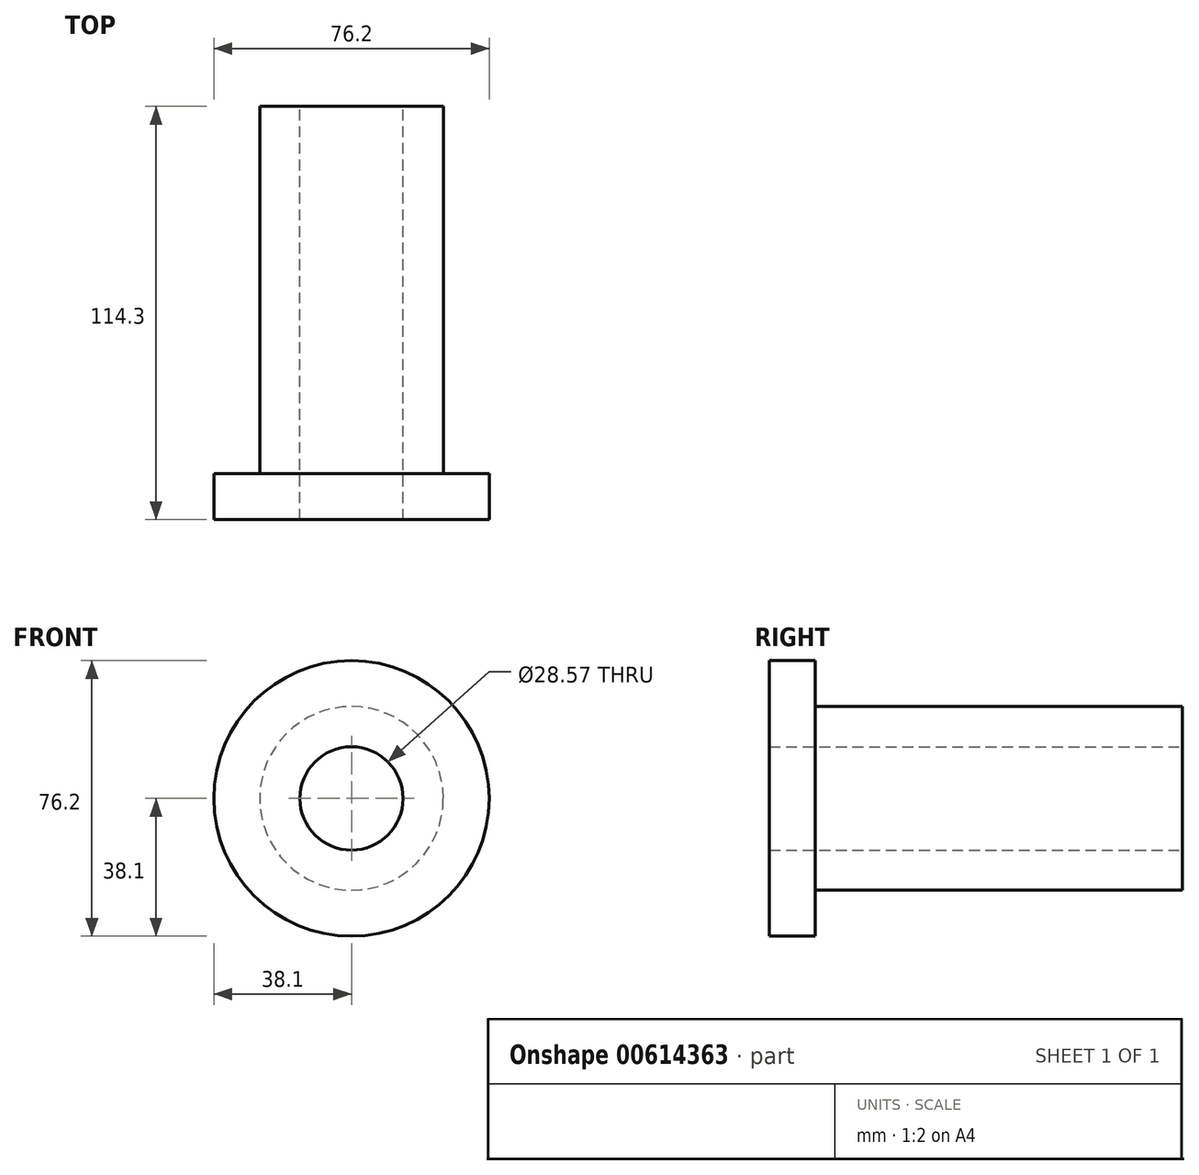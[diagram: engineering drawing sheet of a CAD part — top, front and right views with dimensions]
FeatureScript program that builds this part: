
annotation { "Feature Type Name" : "Feature", "Feature Type Description" : "" }
export const myFeature = defineFeature(function(context is Context, id is Id, definition is map)
    precondition{}
    {
        {
            var Q0;
            Q0=qCreatedBy(makeId("Front.planeOp"),FACE);
            var sketch = newSketch(context, id + "F0", { "sketchPlane" : qUnion([Q0])});
            skCircle(sketch, "E0", {"center": v(0, 0) * mm, "radius": 25.4 * mm});
            skCircle(sketch, "E1", {"center": v(0, 0) * mm, "radius": 14.29 * mm});
            skSolve(sketch);
        }
        {
            var Q0;
            Q0 = qSketchRegion(id + "F0", true);
            extrude(context, id + "F1", {"entities" : qUnion([Q0]), "depth" : 114.3 * mm, "offsetDistance" : 25.4 * mm});
        }
        {
            var Q0;
            Q0=makeQuery(id+"F1.opExtrude","CAP_FACE",FACE,{"disambiguationData":[OSD([sQuery(id+"F0.wireOp",EDGE,"E0"),sQuery(id+"F0.wireOp",EDGE,"E1")])],"isStart":false});
            var sketch = newSketch(context, id + "F2", { "sketchPlane" : qUnion([Q0])});
            skCircle(sketch, "E2.0", {"center": v(0, 0) * mm, "radius": 38.1 * mm});
            skSolve(sketch);
        }
        {
            var Q0;
            Q0=makeQuery(id+"F2.imprint","IMPRINT",FACE,{"disambiguationData":[TD([[makeQuery(id+"F2.imprint","IMPRINT",EDGE,{"derivedFrom":sQuery(id+"F2.wireOp",EDGE,"E2.0")}),1.0]])]});
            extrude(context, id + "F3", {"entities" : qUnion([Q0]), "operationType" : NewBodyOperationType.ADD, "oppositeDirection" : true, "depth" : 12.7 * mm, "offsetDistance" : 25.4 * mm});
        }
    });
